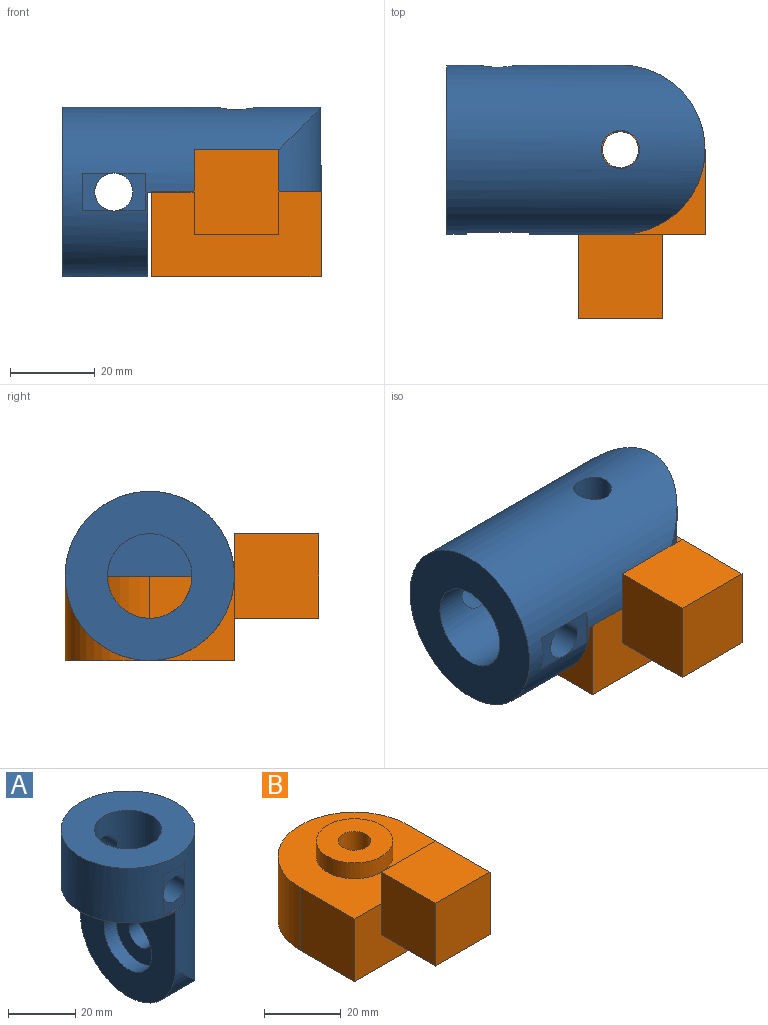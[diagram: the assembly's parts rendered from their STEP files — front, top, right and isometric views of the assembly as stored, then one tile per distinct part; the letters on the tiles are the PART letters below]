
ASSEMBLY  parts=2 mates=1
PART A: 16 faces, bbox 40.1x40x61.1 mm
  f0: cylinder r=20mm len=61.07mm, axis (0,0,-1), area 4370.1mm2, adj f1,f3,f4,f5,f6,f10,f11,f12
  f1: cylinder r=4.5mm len=10.57mm, axis (0,-1,0), area 283.5mm2, adj f0,f2,f12,f15
  f2: cylinder r=10mm len=20mm, axis (0,0,1), area 1125.8mm2, adj f1,f3,f4,f9,f11
  f3: plane 40x20mm, normal (0,0,-1), area 471.2mm2, adj f0,f2,f5
  f4: plane 40x40mm, normal (0,0,1), area 942.5mm2, adj f0,f2
  f5: plane 41x40mm, normal (-1,0,0), area 1154.2mm2, adj f0,f3,f6,f7,f9
  f6: cylinder r=20mm len=40mm, axis (-1,0,0), area 800mm2, adj f0,f5
  f7: cylinder r=10mm len=20mm, axis (-1,0,0), area 314.2mm2, adj f5,f8
  f8: plane 20x20mm, normal (-1,0,0), area 250.5mm2, adj f7,f10
  f9: plane 20x10mm, normal (0,0,1), area 157.1mm2, adj f2,f5
  f10: cylinder r=4.5mm len=15mm, axis (-1,0,0), area 416.9mm2, adj f0,f8
  f11: cylinder r=4.5mm len=11.07mm, axis (0,-1,0), area 290.4mm2, adj f0,f2
  f12: plane 8.89x6.79mm, normal (0,-1,0), area 34.9mm2, adj f0,f1,f13
  f13: plane 8.89x0.5mm, normal (0,0,1), area 3mm2, adj f0,f12
  f14: plane 8.89x0.5mm, normal (0,0,-1), area 3mm2, adj f0,f15
  f15: plane 8.89x6.79mm, normal (0,-1,0), area 34.9mm2, adj f0,f1,f14
PART B: 15 faces, bbox 40x60x30 mm
  f0: plane 40x40mm, normal (0,0,-1), area 1371.6mm2, adj f2,f3,f9,f13,f14
  f1: plane 40x40mm, normal (0,0,1), area 1114.2mm2, adj f2,f3,f7,f9,f11,f14
  f2: plane 20x20mm, normal (-1,0,0), area 400mm2, adj f0,f1,f9,f14
  f3: plane 20x20mm, normal (1,0,0), area 400mm2, adj f0,f1,f9,f14
  f4: plane 20x20mm, normal (0,-1,0), area 400mm2, adj f5,f6,f8,f10
  f5: plane 20x20mm, normal (1,0,0), area 400mm2, adj f4,f7,f8,f9,f10
  f6: plane 20x20mm, normal (-1,0,0), area 400mm2, adj f4,f7,f8,f9,f10
  f7: plane 20x10mm, normal (0,1,0), area 200mm2, adj f1,f5,f6,f8
  f8: plane 20x20mm, normal (0,0,1), area 400mm2, adj f4,f5,f6,f7
  f9: plane 40x20mm, normal (0,-1,0), area 600mm2, adj f0,f1,f2,f3,f5,f6,f10
  f10: plane 20x20mm, normal (0,0,-1), area 400mm2, adj f4,f5,f6,f9
  f11: cylinder r=10mm len=20mm, axis (0,0,-1), area 314.2mm2, adj f1,f12
  f12: plane 20x20mm, normal (0,0,1), area 257.4mm2, adj f11,f13
  f13: cylinder r=4.25mm len=25mm, axis (0,0,1), area 667.6mm2, adj f0,f12
  f14: cylinder r=20mm len=40mm, axis (0,0,1), area 1256.6mm2, adj f0,f1,f2,f3
PLACE A rot(axis=(0,-1,0),90deg) t=(-51.49,-12.7,5.08)mm
PLACE B t=(-75.49,7.3,5.08)mm
MATE slider A.f6 <-> B.f11  axis (0,0,-1) through (-75.49,-12.7,5.08)mm
